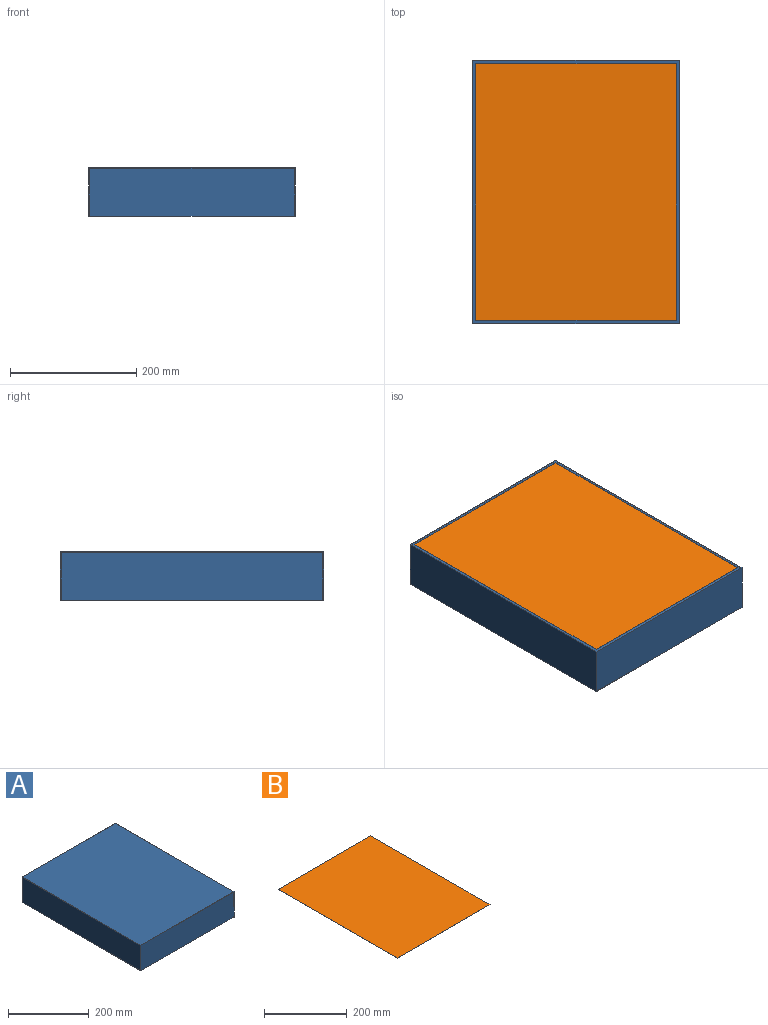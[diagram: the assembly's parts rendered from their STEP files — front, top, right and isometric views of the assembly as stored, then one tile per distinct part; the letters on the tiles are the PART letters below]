
ASSEMBLY  parts=2 mates=1
PART A: 11 faces, bbox 327x417x77 mm
  f0: plane 327x77mm, normal (0,1,0), area 25179mm2, adj f1,f3,f4,f5
  f1: plane 417x77mm, normal (-1,0,0), area 32109mm2, adj f0,f2,f4,f5
  f2: plane 327x77mm, normal (0,-1,0), area 25179mm2, adj f1,f3,f4,f5
  f3: plane 417x77mm, normal (1,0,0), area 32109mm2, adj f0,f2,f4,f5
  f4: plane 417x327mm, normal (0,0,1), area 136359mm2, adj f0,f1,f2,f3
  f5: plane 417x327mm, normal (0,0,-1), area 1779.8mm2, adj f0,f1,f2,f3,f6,f7,f8,f9
  f6: plane 324.6x75.8mm, normal (0,-1,0), area 24604.7mm2, adj f5,f7,f9,f10
  f7: plane 414.6x75.8mm, normal (-1,0,0), area 31426.7mm2, adj f5,f6,f8,f10
  f8: plane 324.6x75.8mm, normal (0,1,0), area 24604.7mm2, adj f5,f7,f9,f10
  f9: plane 414.6x75.8mm, normal (1,0,0), area 31426.7mm2, adj f5,f6,f8,f10
  f10: plane 414.6x324.6mm, normal (0,0,-1), area 134579.2mm2, adj f6,f7,f8,f9
PART B: 6 faces, bbox 317x407x0.3 mm
  f0: plane 317x0.25mm, normal (0,-1,0), area 79.2mm2, adj f1,f3,f4,f5
  f1: plane 407x0.25mm, normal (1,0,0), area 101.7mm2, adj f0,f2,f4,f5
  f2: plane 317x0.25mm, normal (0,1,0), area 79.2mm2, adj f1,f3,f4,f5
  f3: plane 407x0.25mm, normal (-1,0,0), area 101.7mm2, adj f0,f2,f4,f5
  f4: plane 407x317mm, normal (0,0,1), area 129019mm2, adj f0,f1,f2,f3
  f5: plane 407x317mm, normal (0,0,-1), area 129019mm2, adj f0,f1,f2,f3
PLACE A t=(11.49,2.56,-89.02)mm
PLACE B t=(11.49,2.56,-12.02)mm
MATE fastened B.f5 <-> A.f4  axis (0,0,-1) through (11.49,2.56,-12.02)mm
